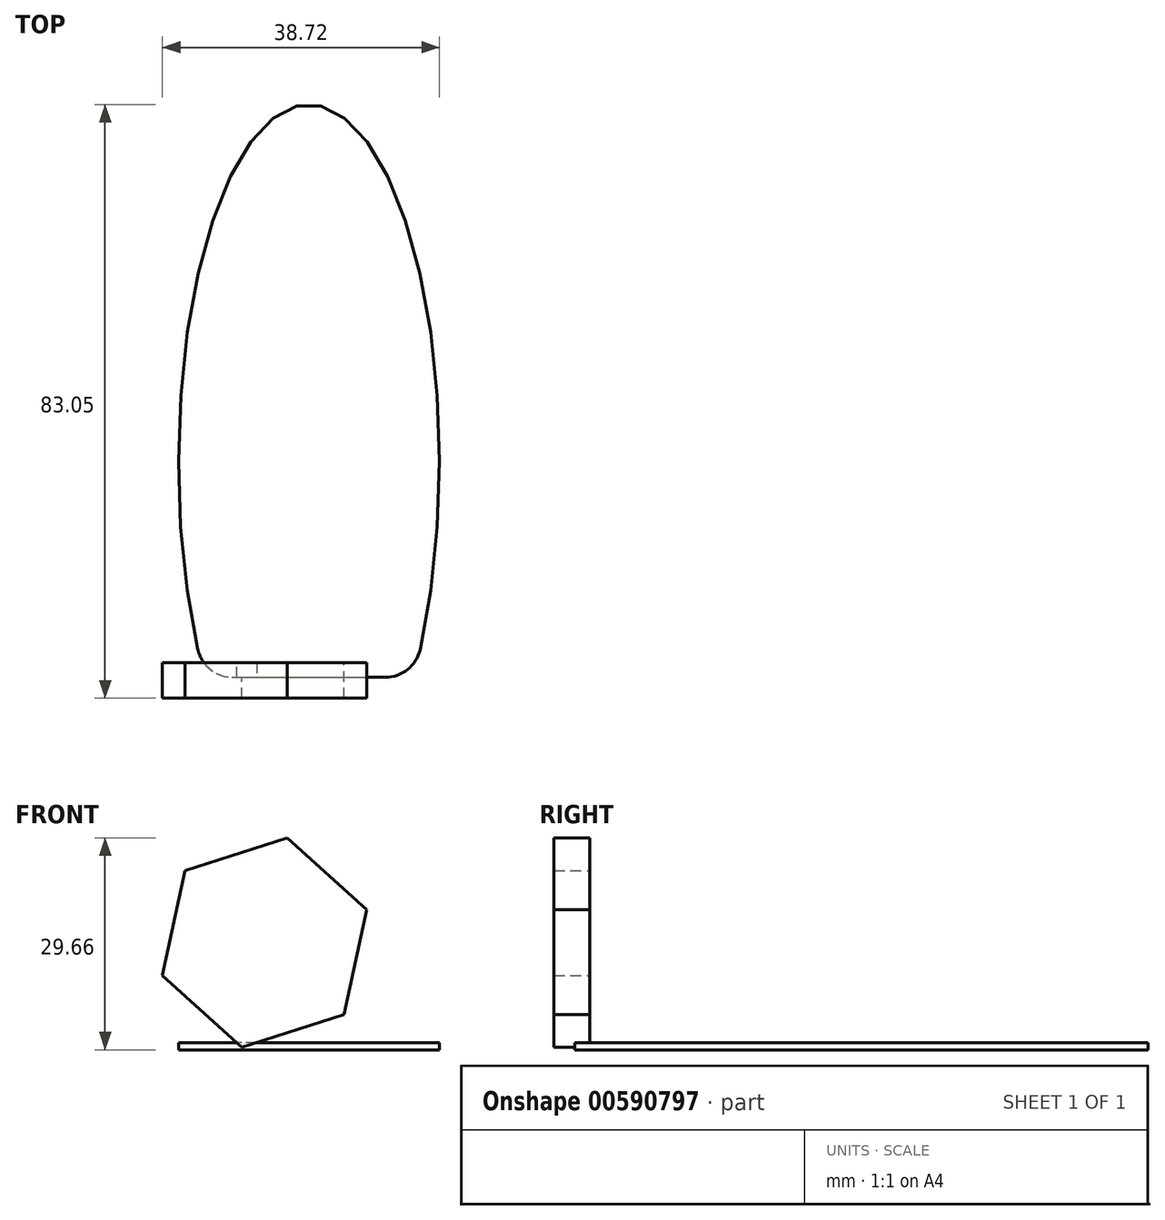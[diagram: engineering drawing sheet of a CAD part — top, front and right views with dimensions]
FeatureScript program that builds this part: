
annotation { "Feature Type Name" : "Feature", "Feature Type Description" : "" }
export const myFeature = defineFeature(function(context is Context, id is Id, definition is map)
    precondition{}
    {
        {
            var Q0;
            Q0=qCreatedBy(makeId("Front.planeOp"),FACE);
            var sketch = newSketch(context, id + "F0", { "sketchPlane" : qUnion([Q0])});
            skLineSegment(sketch, "E0.0", {"start": v(3.18, 14.66) * mm, "end": v(14.28, 4.58) * mm});
            skLineSegment(sketch, "E0.1", {"start": v(14.28, 4.58) * mm, "end": v(11.1, -10.08) * mm});
            skLineSegment(sketch, "E0.2", {"start": v(11.1, -10.08) * mm, "end": v(-3.18, -14.66) * mm});
            skLineSegment(sketch, "E0.3", {"start": v(-3.18, -14.66) * mm, "end": v(-14.28, -4.58) * mm});
            skLineSegment(sketch, "E0.4", {"start": v(-14.28, -4.58) * mm, "end": v(-11.1, 10.08) * mm});
            skLineSegment(sketch, "E0.5", {"start": v(-11.1, 10.08) * mm, "end": v(3.18, 14.66) * mm});
            skSolve(sketch);
        }
        {
            var Q0;
            Q0=makeQuery(id+"F0.imprint","IMPRINT",FACE,{"disambiguationData":[TD([[makeQuery(id+"F0.imprint","IMPRINT",EDGE,{"derivedFrom":sQuery(id+"F0.wireOp",EDGE,"E0.0")}),-1.0]])]});
            extrude(context, id + "F1", {"entities" : qUnion([Q0]), "depth" : 5 * mm, "offsetDistance" : 25 * mm});
        }
        {
            var Q0;
            Q0=qCreatedBy(makeId("Top.planeOp"),FACE);
            cPlane(context, id + "F2", {"entities" : qUnion([Q0]), "cplaneType" : CPlaneType.OFFSET, "offset" : 15 * mm, "oppositeDirection" : true, "width" : 150 * mm, "height" : 150 * mm});
        }
        {
            var Q0;
            Q0=qCreatedBy(id+"F2.planeOp",FACE);
            var sketch = newSketch(context, id + "F3", { "sketchPlane" : qUnion([Q0])});
            skEllipse(sketch, "E1", {"center": v(6.2, 28.05) * mm, "majorRadius": 50 * mm, "minorRadius": 18.24 * mm, "majorAxis": v(0, 1)});
            skLineSegment(sketch, "E2", {"start": v(6.2, -2.06) * mm, "end": v(6.2, 67.67) * mm, "construction": true});
            skLineSegment(sketch, "E3", {"start": v(-8.36, -2.06) * mm, "end": v(20.76, -2.06) * mm});
            skSolve(sketch);
        }
        {
            var Q0;
            {var subQ0=sQuery(id+"F3.wireOp",EDGE,"E3");Q0=makeQuery(id+"F3.imprint","IMPRINT",FACE,{"disambiguationData":[TD([[makeQuery(id+"F3.imprint","IMPRINT",EDGE,{"derivedFrom":subQ0}),1.0]])]});}
            extrude(context, id + "F4", {"entities" : qUnion([Q0]), "operationType" : NewBodyOperationType.ADD, "depth" : 1 * mm, "offsetDistance" : 25 * mm});
        }
        {
            var Q0;
            {var subQ0=sQuery(id+"F3.wireOp",EDGE,"E3");var subQ1=sQuery(id+"F3.wireOp",EDGE,"E1");Q0=makeQuery(id+"F4.opExtrude","SWEPT_EDGE",EDGE,{"disambiguationData":[OSD([subQ1,subQ0]),TDD([makeQuery(id+"F3.imprint","INTERSECT",VERTEX,{"disambiguationData":[OD(1.0)],"derivedFrom":[subQ1,subQ0]})])]});}
            var Q1;
            {var subQ0=sQuery(id+"F3.wireOp",EDGE,"E3");var subQ1=sQuery(id+"F3.wireOp",EDGE,"E1");Q1=makeQuery(id+"F4.opExtrude","SWEPT_EDGE",EDGE,{"disambiguationData":[OSD([subQ1,subQ0]),TDD([makeQuery(id+"F3.imprint","INTERSECT",VERTEX,{"disambiguationData":[OD(0.0)],"derivedFrom":[subQ1,subQ0]})])]});}
            fillet(context, id + "F5", {"entities" : qUnion([Q0, Q1]), "radius" : 5 * mm, "tangentPropagation" : true, "allowEdgeOverflow" : false});
        }
    });
